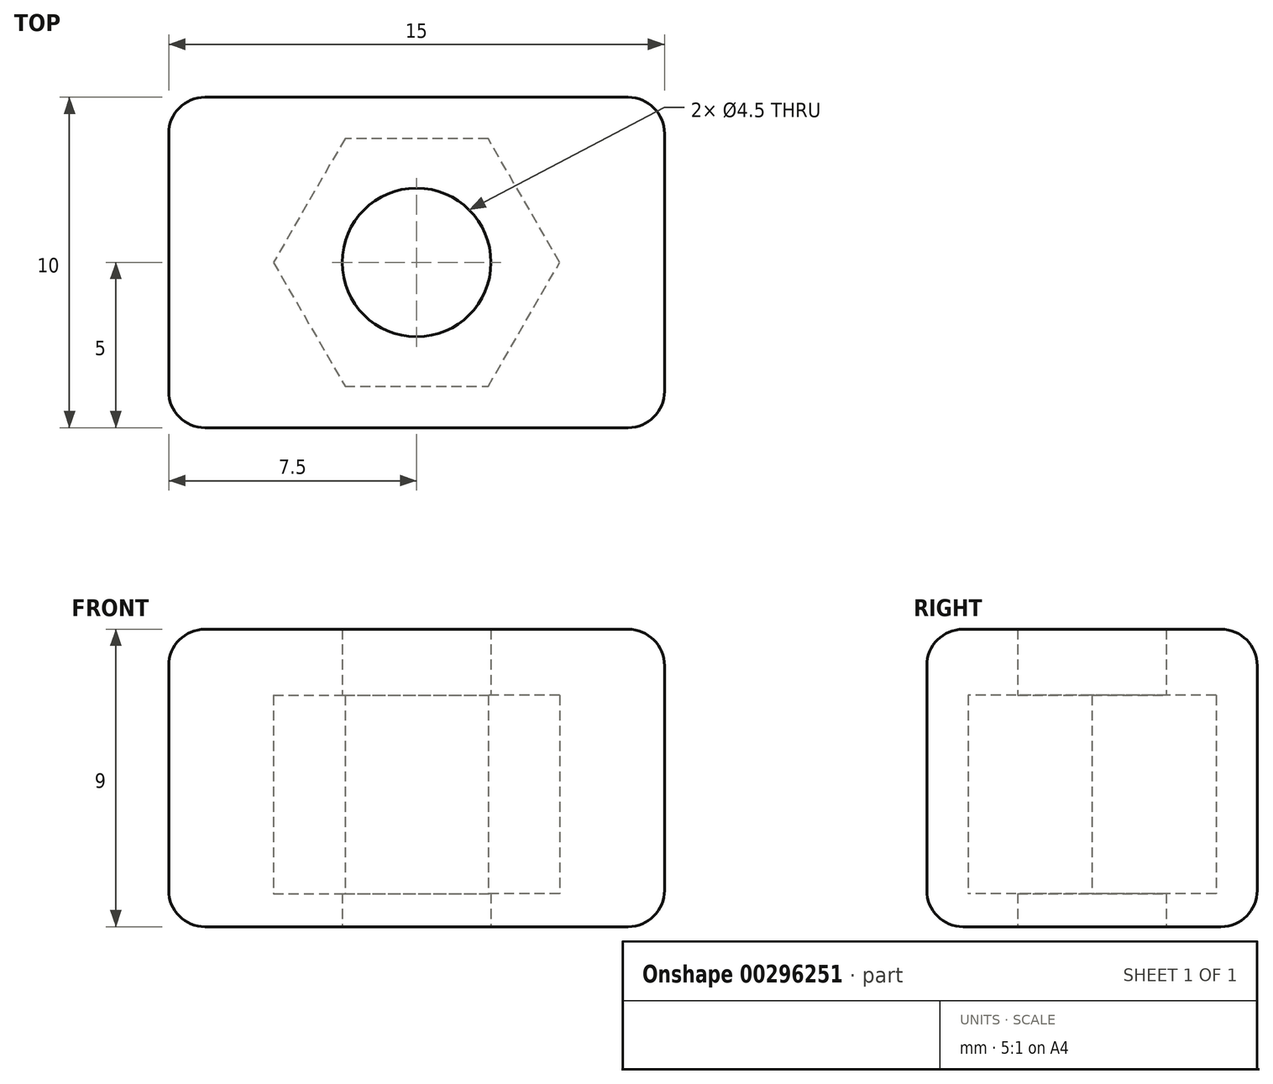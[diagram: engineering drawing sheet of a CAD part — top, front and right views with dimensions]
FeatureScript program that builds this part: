
annotation { "Feature Type Name" : "Feature", "Feature Type Description" : "" }
export const myFeature = defineFeature(function(context is Context, id is Id, definition is map)
    precondition{}
    {
        {
            var Q0;
            Q0=qCreatedBy(makeId("Front.planeOp"),FACE);
            var sketch = newSketch(context, id + "F0", { "sketchPlane" : qUnion([Q0])});
            skLineSegment(sketch, "E0.bottom", {"start": v(0, 0) * mm, "end": v(15, 0) * mm});
            skLineSegment(sketch, "E0.top", {"start": v(0, 9) * mm, "end": v(15, 9) * mm});
            skLineSegment(sketch, "E0.left", {"start": v(0, 0) * mm, "end": v(0, 9) * mm});
            skLineSegment(sketch, "E0.right", {"start": v(15, 0) * mm, "end": v(15, 9) * mm});
            skLineSegment(sketch, "E1.bottom", {"start": v(15, 9) * mm, "end": v(12.7, 9) * mm});
            skLineSegment(sketch, "E1.top", {"start": v(15, 17) * mm, "end": v(12.7, 17) * mm});
            skLineSegment(sketch, "E1.left", {"start": v(15, 9) * mm, "end": v(15, 17) * mm});
            skLineSegment(sketch, "E1.right", {"start": v(12.7, 9) * mm, "end": v(12.7, 17) * mm});
            skLineSegment(sketch, "E2.bottom", {"start": v(0, 9) * mm, "end": v(2.3, 9) * mm});
            skLineSegment(sketch, "E2.top", {"start": v(0, 17) * mm, "end": v(2.3, 17) * mm});
            skLineSegment(sketch, "E2.left", {"start": v(0, 9) * mm, "end": v(0, 17) * mm});
            skLineSegment(sketch, "E2.right", {"start": v(2.3, 9) * mm, "end": v(2.3, 17) * mm});
            skSolve(sketch);
        }
        {
            var Q0;
            Q0=makeQuery(id+"F0.imprint","IMPRINT",FACE,{"disambiguationData":[TD([[makeQuery(id+"F0.imprint","IMPRINT",EDGE,{"derivedFrom":sQuery(id+"F0.wireOp",EDGE,"E2.bottom")}),1.0]])]});
            var Q1;
            Q1=makeQuery(id+"F0.imprint","IMPRINT",FACE,{"disambiguationData":[TD([[makeQuery(id+"F0.imprint","IMPRINT",EDGE,{"derivedFrom":sQuery(id+"F0.wireOp",EDGE,"E0.bottom")}),1.0]])]});
            var Q2;
            Q2=makeQuery(id+"F0.imprint","IMPRINT",FACE,{"disambiguationData":[TD([[makeQuery(id+"F0.imprint","IMPRINT",EDGE,{"derivedFrom":sQuery(id+"F0.wireOp",EDGE,"E1.bottom")}),-1.0]])]});
            extrude(context, id + "F1", {"entities" : qUnion([Q0, Q1, Q2]), "depth" : 10 * mm});
        }
        {
            var Q0;
            Q0=makeQuery(id+"F1.opExtrude","SWEPT_FACE",FACE,{"disambiguationData":[OSD([sQuery(id+"F0.wireOp",EDGE,"E0.bottom")])]});
            var sketch = newSketch(context, id + "F2", { "sketchPlane" : qUnion([Q0])});
            skCircle(sketch, "E3", {"center": v(7.5, 5) * mm, "radius": 2.25 * mm});
            skPoint(sketch, "E3.centerSnap0", {"position": v(7.5, 10) * mm});
            skPoint(sketch, "E3.centerSnap1", {"position": v(0, 5) * mm});
            skCircle(sketch, "E4.cCircle", {"center": v(7.5, 5) * mm, "radius": 3.75 * mm, "construction": true});
            skLineSegment(sketch, "E4.0", {"start": v(9.67, 1.25) * mm, "end": v(5.33, 1.25) * mm});
            skLineSegment(sketch, "E4.1", {"start": v(5.33, 1.25) * mm, "end": v(3.17, 5) * mm});
            skLineSegment(sketch, "E4.2", {"start": v(3.17, 5) * mm, "end": v(5.33, 8.75) * mm});
            skLineSegment(sketch, "E4.3", {"start": v(5.33, 8.75) * mm, "end": v(9.67, 8.75) * mm});
            skLineSegment(sketch, "E4.4", {"start": v(9.67, 8.75) * mm, "end": v(11.83, 5) * mm});
            skLineSegment(sketch, "E4.5", {"start": v(11.83, 5) * mm, "end": v(9.67, 1.25) * mm});
            skPoint(sketch, "E4.0.midPoint", {"position": v(7.5, 1.25) * mm});
            skPoint(sketch, "E5", {"position": v(7.5, 0) * mm});
            skLineSegment(sketch, "E6", {"start": v(9.67, 1.25) * mm, "end": v(5.33, 8.75) * mm});
            skSolve(sketch);
        }
        {
            var Q0;
            Q0=makeQuery(id+"F2.imprint","IMPRINT",FACE,{"disambiguationData":[TD([[makeQuery(id+"F2.imprint","IMPRINT",EDGE,{"derivedFrom":sQuery(id+"F2.wireOp",EDGE,"E3")}),1.0]])]});
            extrude(context, id + "F3", {"entities" : qUnion([Q0]), "operationType" : NewBodyOperationType.REMOVE, "endBound" : BoundingType.THROUGH_ALL, "oppositeDirection" : true, "depth" : 25 * mm});
        }
        {
            var Q0;
            Q0=makeQuery(id+"F2.imprint","IMPRINT",FACE,{"disambiguationData":[TD([[makeQuery(id+"F2.imprint","IMPRINT",EDGE,{"derivedFrom":sQuery(id+"F2.wireOp",EDGE,"E3")}),-1.0]])]});
            extrude(context, id + "F4", {"entities" : qUnion([Q0]), "operationType" : NewBodyOperationType.REMOVE, "oppositeDirection" : true, "depth" : 7 * mm});
        }
        {
            var Q0;
            {var subQ1=sQuery(id+"F2.wireOp",EDGE,"E4.0");Q0=makeQuery(id+"F2.imprint","IMPRINT",FACE,{"disambiguationData":[TD([[makeQuery(id+"F2.imprint","IMPRINT",EDGE,{"derivedFrom":subQ1}),-1.0]])]});}
            var Q1;
            {var subQ1=sQuery(id+"F2.wireOp",EDGE,"E4.3");Q1=makeQuery(id+"F2.imprint","IMPRINT",FACE,{"disambiguationData":[TD([[makeQuery(id+"F2.imprint","IMPRINT",EDGE,{"derivedFrom":subQ1}),-1.0]])]});}
            extrude(context, id + "F5", {"entities" : qUnion([Q0, Q1]), "operationType" : NewBodyOperationType.ADD, "oppositeDirection" : true, "depth" : 1 * mm});
        }
        {
            var Q0;
            Q0=makeQuery(id+"F1.opExtrude","CAP_FACE",FACE,{"disambiguationData":[OSD([sQuery(id+"F0.wireOp",EDGE,"E0.bottom"),sQuery(id+"F0.wireOp",EDGE,"E0.top"),sQuery(id+"F0.wireOp",EDGE,"E0.left"),sQuery(id+"F0.wireOp",EDGE,"E0.right"),sQuery(id+"F0.wireOp",EDGE,"E1.top"),sQuery(id+"F0.wireOp",EDGE,"E1.left"),sQuery(id+"F0.wireOp",EDGE,"E1.right"),sQuery(id+"F0.wireOp",EDGE,"E2.top"),sQuery(id+"F0.wireOp",EDGE,"E2.left"),sQuery(id+"F0.wireOp",EDGE,"E2.right")])],"isStart":true});
            var Q1;
            Q1=makeQuery(id+"F1.opExtrude","CAP_FACE",FACE,{"disambiguationData":[OSD([sQuery(id+"F0.wireOp",EDGE,"E0.bottom"),sQuery(id+"F0.wireOp",EDGE,"E0.top"),sQuery(id+"F0.wireOp",EDGE,"E0.left"),sQuery(id+"F0.wireOp",EDGE,"E0.right"),sQuery(id+"F0.wireOp",EDGE,"E1.top"),sQuery(id+"F0.wireOp",EDGE,"E1.left"),sQuery(id+"F0.wireOp",EDGE,"E1.right"),sQuery(id+"F0.wireOp",EDGE,"E2.top"),sQuery(id+"F0.wireOp",EDGE,"E2.left"),sQuery(id+"F0.wireOp",EDGE,"E2.right")])],"isStart":false});
            var Q2;
            Q2=makeQuery(id+"F1.opExtrude","SWEPT_FACE",FACE,{"disambiguationData":[OSD([sQuery(id+"F0.wireOp",EDGE,"E0.right"),sQuery(id+"F0.wireOp",EDGE,"E1.left")])]});
            var Q3;
            Q3=makeQuery(id+"F1.opExtrude","SWEPT_FACE",FACE,{"disambiguationData":[OSD([sQuery(id+"F0.wireOp",EDGE,"E0.left"),sQuery(id+"F0.wireOp",EDGE,"E2.left")])]});
            var Q4;
            Q4=makeQuery(id+"F1.opExtrude","SWEPT_FACE",FACE,{"disambiguationData":[OSD([sQuery(id+"F0.wireOp",EDGE,"E1.right")])]});
            var Q5;
            Q5=makeQuery(id+"F1.opExtrude","SWEPT_FACE",FACE,{"disambiguationData":[OSD([sQuery(id+"F0.wireOp",EDGE,"E2.right")])]});
            fillet(context, id + "F6", {"entities" : qUnion([Q0, Q1, Q2, Q3, Q4, Q5]), "radius" : 1.1 * mm, "tangentPropagation" : true, "allowEdgeOverflow" : false});
        }
    });
